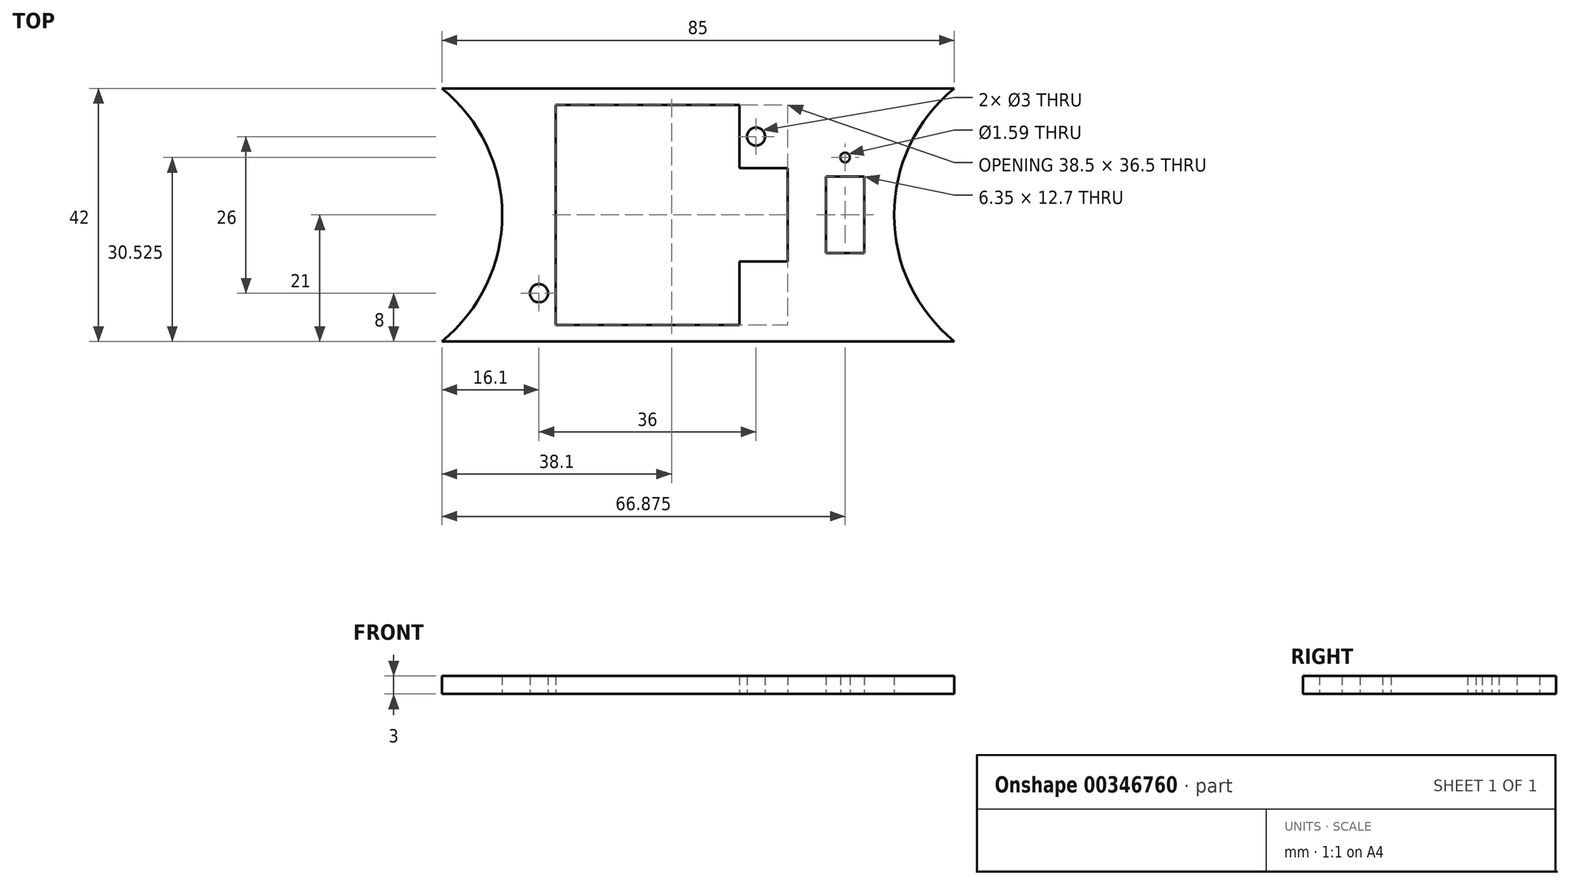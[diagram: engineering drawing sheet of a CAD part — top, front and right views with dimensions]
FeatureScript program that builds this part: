
annotation { "Feature Type Name" : "Feature", "Feature Type Description" : "" }
export const myFeature = defineFeature(function(context is Context, id is Id, definition is map)
    precondition{}
    {
        {
            var Q0;
            Q0=qCreatedBy(makeId("Top.planeOp"),FACE);
            var sketch = newSketch(context, id + "F0", { "sketchPlane" : qUnion([Q0])});
            skLineSegment(sketch, "E0.bottom", {"start": v(-6, 9.53) * mm, "end": v(6, 9.53) * mm});
            skLineSegment(sketch, "E0.top", {"start": v(-6, -9.53) * mm, "end": v(6, -9.53) * mm});
            skLineSegment(sketch, "E0.left", {"start": v(-6, 9.53) * mm, "end": v(-6, -9.53) * mm});
            skLineSegment(sketch, "E0.right", {"start": v(6, 9.53) * mm, "end": v(6, -9.52) * mm});
            skPoint(sketch, "E0.middle", {"position": v(0, 0) * mm});
            skPoint(sketch, "E1.endSnap0", {"position": v(6, 0) * mm});
            skLineSegment(sketch, "E2", {"start": v(-48, 5) * mm, "end": v(-18, 5) * mm});
            skLineSegment(sketch, "E3", {"start": v(-54.35, -12) * mm, "end": v(-54.35, -5) * mm});
            skLineSegment(sketch, "E4", {"start": v(-54.35, -5) * mm, "end": v(-48, -5) * mm});
            skLineSegment(sketch, "E5", {"start": v(-54.35, -12) * mm, "end": v(-18, -12) * mm});
            skLineSegment(sketch, "E6", {"start": v(-18, 5) * mm, "end": v(-18, -12) * mm});
            skLineSegment(sketch, "E7", {"start": v(-48, -5) * mm, "end": v(-18, -5) * mm, "construction": true});
            skLineSegment(sketch, "E8", {"start": v(0, 9.53) * mm, "end": v(0, -9.53) * mm, "construction": true});
            skLineSegment(sketch, "E9.bottom", {"start": v(-61.75, 14.31) * mm, "end": v(61.75, 14.31) * mm});
            skLineSegment(sketch, "E9.top", {"start": v(-61.75, -14.31) * mm, "end": v(61.75, -14.31) * mm});
            skLineSegment(sketch, "E10", {"start": v(-48, 5) * mm, "end": v(-48, -5) * mm});
            skCircle(sketch, "E11", {"center": v(-39.45, 0) * mm, "radius": 2.5 * mm, "construction": true});
            skLineSegment(sketch, "E12.MirrorCS", {"start": v(0, -9.52) * mm, "end": v(0, 9.53) * mm, "construction": true});
            skLineSegment(sketch, "E13", {"start": v(0, 0) * mm, "end": v(-48, 0) * mm, "construction": true});
            skLineSegment(sketch, "E14.MirrorCS", {"start": v(0, 9.52) * mm, "end": v(0, -9.53) * mm, "construction": true});
            skLineSegment(sketch, "E15", {"start": v(-33, 5) * mm, "end": v(-33, -12) * mm, "construction": true});
            skCircle(sketch, "E16", {"center": v(-51, 0) * mm, "radius": 0.89 * mm});
            skCircle(sketch, "E17.MirrorC", {"center": v(-15, 0) * mm, "radius": 0.89 * mm});
            skLineSegment(sketch, "E18.MirrorCS", {"start": v(0, 0) * mm, "end": v(48, 0) * mm, "construction": true});
            skCircle(sketch, "E19.MirrorC", {"center": v(51, 0) * mm, "radius": 0.89 * mm});
            skLineSegment(sketch, "E20", {"start": v(61.75, 14.31) * mm, "end": v(74.45, 14.31) * mm});
            skLineSegment(sketch, "E21", {"start": v(61.75, -14.31) * mm, "end": v(74.45, -14.31) * mm});
            skLineSegment(sketch, "E22", {"start": v(-61.75, 14.31) * mm, "end": v(-74.45, 14.31) * mm});
            skLineSegment(sketch, "E23", {"start": v(-61.75, -14.31) * mm, "end": v(-74.45, -14.31) * mm});
            skArc(sketch, "E24", {"start": v(74.45, 14.31) * mm, "mid": v(61.75, 0) * mm, "end": v(74.45, -14.31) * mm});
            skPoint(sketch, "E24.second.point", {"position": v(61.75, 0) * mm});
            skArc(sketch, "E25", {"start": v(-74.45, -14.31) * mm, "mid": v(-61.75, 0) * mm, "end": v(-74.45, 14.31) * mm});
            skPoint(sketch, "E25.second.point", {"position": v(-61.75, 0) * mm});
            skLineSegment(sketch, "E26", {"start": v(6, 9.53) * mm, "end": v(31, 9.53) * mm});
            skLineSegment(sketch, "E27", {"start": v(31, 9.53) * mm, "end": v(31, -9.52) * mm});
            skLineSegment(sketch, "E28", {"start": v(31, -9.52) * mm, "end": v(6, -9.53) * mm});
            skSolve(sketch);
        }
        {
            var Q0;
            Q0=qCreatedBy(makeId("Top.planeOp"),FACE);
            var sketch = newSketch(context, id + "F1", { "sketchPlane" : qUnion([Q0])});
            skLineSegment(sketch, "E29.bottom", {"start": v(-15.25, 5.25) * mm, "end": v(15.25, 5.25) * mm});
            skLineSegment(sketch, "E29.top", {"start": v(-15.25, -5.25) * mm, "end": v(15.25, -5.25) * mm, "construction": true});
            skLineSegment(sketch, "E29.left", {"start": v(-15.25, 5.25) * mm, "end": v(-15.25, -5.25) * mm});
            skLineSegment(sketch, "E29.right", {"start": v(15.25, 5.25) * mm, "end": v(15.25, -5.25) * mm});
            skPoint(sketch, "E29.middle", {"position": v(0, 0) * mm});
            skLineSegment(sketch, "E30", {"start": v(15.25, -5.25) * mm, "end": v(23.25, -5.25) * mm});
            skLineSegment(sketch, "E31", {"start": v(23.25, -20.75) * mm, "end": v(15.25, -20.75) * mm});
            skLineSegment(sketch, "E32", {"start": v(-15.25, -20.75) * mm, "end": v(-15.25, -31.25) * mm});
            skLineSegment(sketch, "E33", {"start": v(-15.25, -31.25) * mm, "end": v(15.25, -31.25) * mm});
            skLineSegment(sketch, "E34", {"start": v(15.25, -31.25) * mm, "end": v(15.25, -20.75) * mm});
            skCircle(sketch, "E35", {"center": v(18, 0) * mm, "radius": 1.5 * mm});
            skLineSegment(sketch, "E36", {"start": v(0, 5.25) * mm, "end": v(0, -31.25) * mm, "construction": true});
            skCircle(sketch, "E37.MirrorC", {"center": v(-18, 0) * mm, "radius": 1.5 * mm});
            skLineSegment(sketch, "E38", {"start": v(-15.25, -13) * mm, "end": v(23.25, -13) * mm, "construction": true});
            skCircle(sketch, "E39.MirrorC", {"center": v(18, -26) * mm, "radius": 1.5 * mm});
            skCircle(sketch, "E40.MirrorC", {"center": v(-18, -26) * mm, "radius": 1.5 * mm});
            skLineSegment(sketch, "E41", {"start": v(23.25, -13) * mm, "end": v(57.76, -13) * mm, "construction": true});
            skLineSegment(sketch, "E42.bottom", {"start": v(35.95, -6.65) * mm, "end": v(29.6, -6.65) * mm});
            skLineSegment(sketch, "E42.top", {"start": v(35.95, -19.35) * mm, "end": v(29.6, -19.35) * mm});
            skLineSegment(sketch, "E42.left", {"start": v(35.95, -6.65) * mm, "end": v(35.95, -19.35) * mm});
            skLineSegment(sketch, "E42.right", {"start": v(29.6, -6.65) * mm, "end": v(29.6, -19.35) * mm});
            skPoint(sketch, "E42.middle", {"position": v(32.78, -13) * mm});
            skCircle(sketch, "E43", {"center": v(32.78, -3.47) * mm, "radius": 0.8 * mm});
            skCircle(sketch, "E44.MirrorC", {"center": v(32.78, -22.52) * mm, "radius": 0.8 * mm});
            skCircle(sketch, "E45", {"center": v(-8.4, 0) * mm, "radius": 2.5 * mm, "construction": true});
            skPoint(sketch, "E45.centerSnap0", {"position": v(-15.25, 0) * mm});
            skCircle(sketch, "E46", {"center": v(8.4, -26) * mm, "radius": 2.5 * mm, "construction": true});
            skLineSegment(sketch, "E47", {"start": v(-18, -26) * mm, "end": v(18, -26) * mm, "construction": true});
            skLineSegment(sketch, "E48", {"start": v(-18, 0) * mm, "end": v(18, 0) * mm, "construction": true});
            skLineSegment(sketch, "E49", {"start": v(-15.25, -5.25) * mm, "end": v(-15.25, -20.75) * mm});
            skLineSegment(sketch, "E50", {"start": v(23.25, -5.25) * mm, "end": v(23.25, -20.75) * mm});
            skSolve(sketch);
        }
        {
            var Q0;
            Q0=qCreatedBy(makeId("Top.planeOp"),FACE);
            var sketch = newSketch(context, id + "F2", { "sketchPlane" : qUnion([Q0])});
            skPoint(sketch, "E51.0", {"position": v(8.4, -26) * mm});
            skPoint(sketch, "E52.0", {"position": v(-8.4, 0) * mm});
            skCircle(sketch, "E53", {"center": v(8.4, -26) * mm, "radius": 3.75 * mm});
            skLineSegment(sketch, "E54", {"start": v(8.4, -26) * mm, "end": v(8.4, 0) * mm, "construction": true});
            skCircle(sketch, "E55", {"center": v(8.4, -19) * mm, "radius": 0.8 * mm});
            skCircle(sketch, "E56.0.1.0", {"center": v(8.4, -16) * mm, "radius": 0.8 * mm});
            skCircle(sketch, "E56.0.2.0", {"center": v(8.4, -13) * mm, "radius": 0.8 * mm});
            skLineSegment(sketch, "E56.direction2", {"start": v(8.4, -19) * mm, "end": v(8.4, -16) * mm, "construction": true});
            skCircle(sketch, "E57.MirrorC", {"center": v(-8.4, -13) * mm, "radius": 0.8 * mm});
            skCircle(sketch, "E58.MirrorC", {"center": v(-8.4, 0) * mm, "radius": 3.75 * mm});
            skCircle(sketch, "E59.MirrorC", {"center": v(-8.4, -7) * mm, "radius": 0.8 * mm});
            skCircle(sketch, "E60.MirrorC", {"center": v(-8.4, -10) * mm, "radius": 0.8 * mm});
            skSolve(sketch);
        }
        {
            var Q0;
            Q0=qCreatedBy(makeId("Top.planeOp"),FACE);
            var sketch = newSketch(context, id + "F3", { "sketchPlane" : qUnion([Q0])});
            skPoint(sketch, "E61.0", {"position": v(8.4, -13) * mm});
            skLineSegment(sketch, "E62.bottom", {"start": v(50.9, -34) * mm, "end": v(-34.1, -34) * mm});
            skLineSegment(sketch, "E62.top", {"start": v(50.9, 8) * mm, "end": v(-34.1, 8) * mm});
            skArc(sketch, "E63", {"start": v(50.9, 8) * mm, "mid": v(40.9, -13) * mm, "end": v(50.9, -34) * mm});
            skPoint(sketch, "E63.third.point", {"position": v(40.9, -13) * mm});
            skArc(sketch, "E64", {"start": v(-34.1, -34) * mm, "mid": v(-24.1, -13) * mm, "end": v(-34.1, 8) * mm});
            skPoint(sketch, "E64.third.point", {"position": v(-24.1, -13) * mm});
            skSolve(sketch);
        }
        {
            var Q0;
            Q0=makeQuery(id+"F3.imprint","IMPRINT",FACE,{"disambiguationData":[TD([[makeQuery(id+"F3.imprint","IMPRINT",EDGE,{"derivedFrom":sQuery(id+"F3.wireOp",EDGE,"E62.bottom")}),-1.0]])]});
            extrude(context, id + "F4", {"entities" : qUnion([Q0]), "depth" : 3 * mm});
        }
        {
            var Q0;
            Q0=makeQuery(id+"F1.imprint","IMPRINT",FACE,{"disambiguationData":[TD([[makeQuery(id+"F1.imprint","IMPRINT",EDGE,{"derivedFrom":sQuery(id+"F1.wireOp",EDGE,"E29.bottom")}),-1.0]])]});
            var Q1;
            Q1=makeQuery(id+"F1.imprint","IMPRINT",FACE,{"disambiguationData":[TD([[makeQuery(id+"F1.imprint","IMPRINT",EDGE,{"derivedFrom":sQuery(id+"F1.wireOp",EDGE,"E37.MirrorC")}),-1.0]])]});
            var Q2;
            Q2=makeQuery(id+"F1.imprint","IMPRINT",FACE,{"disambiguationData":[TD([[makeQuery(id+"F1.imprint","IMPRINT",EDGE,{"derivedFrom":sQuery(id+"F1.wireOp",EDGE,"E35")}),1.0]])]});
            var Q3;
            Q3=makeQuery(id+"F1.imprint","IMPRINT",FACE,{"disambiguationData":[TD([[makeQuery(id+"F1.imprint","IMPRINT",EDGE,{"derivedFrom":sQuery(id+"F1.wireOp",EDGE,"E39.MirrorC")}),-1.0]])]});
            var Q4;
            Q4=makeQuery(id+"F1.imprint","IMPRINT",FACE,{"disambiguationData":[TD([[makeQuery(id+"F1.imprint","IMPRINT",EDGE,{"derivedFrom":sQuery(id+"F1.wireOp",EDGE,"E40.MirrorC")}),1.0]])]});
            var Q5;
            Q5=makeQuery(id+"F1.imprint","IMPRINT",FACE,{"disambiguationData":[TD([[makeQuery(id+"F1.imprint","IMPRINT",EDGE,{"derivedFrom":sQuery(id+"F1.wireOp",EDGE,"E42.bottom")}),1.0]])]});
            var Q6;
            Q6=makeQuery(id+"F1.imprint","IMPRINT",FACE,{"disambiguationData":[TD([[makeQuery(id+"F1.imprint","IMPRINT",EDGE,{"derivedFrom":sQuery(id+"F1.wireOp",EDGE,"E44.MirrorC")}),-1.0]])]});
            var Q7;
            Q7=makeQuery(id+"F1.imprint","IMPRINT",FACE,{"disambiguationData":[TD([[makeQuery(id+"F1.imprint","IMPRINT",EDGE,{"derivedFrom":sQuery(id+"F1.wireOp",EDGE,"E43")}),1.0]])]});
            extrude(context, id + "F5", {"entities" : qUnion([Q0, Q1, Q2, Q3, Q4, Q5, Q6, Q7]), "operationType" : NewBodyOperationType.REMOVE, "endBound" : BoundingType.THROUGH_ALL, "depth" : 25 * mm});
        }
    });
